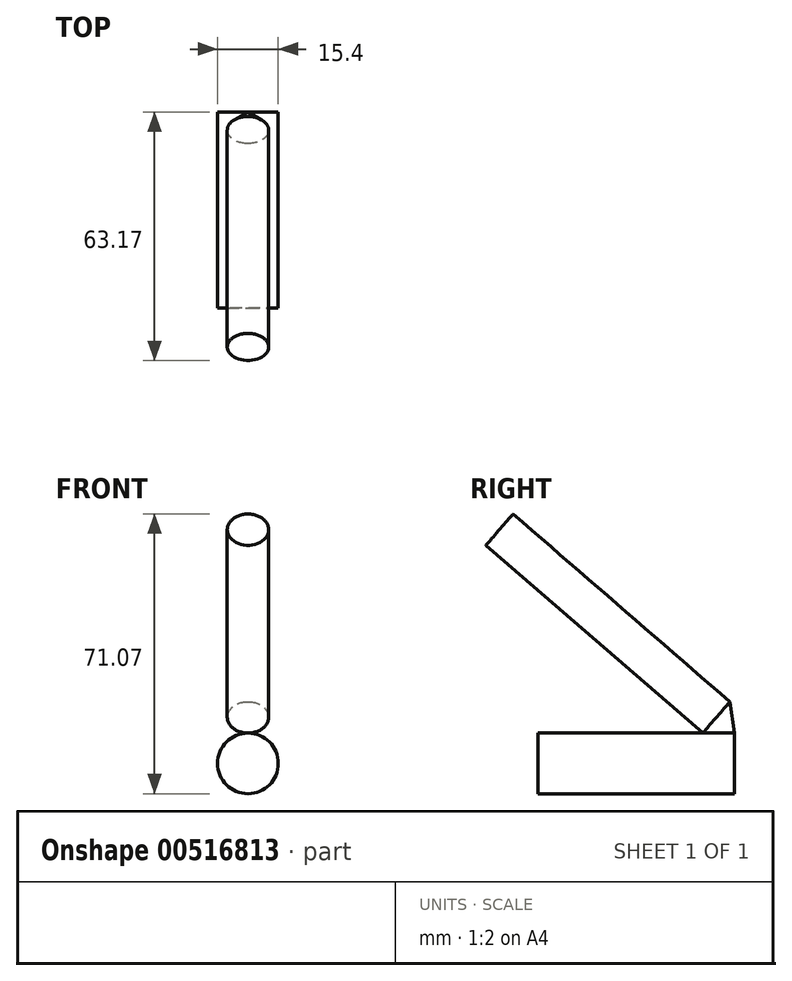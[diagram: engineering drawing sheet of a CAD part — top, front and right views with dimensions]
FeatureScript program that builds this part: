
annotation { "Feature Type Name" : "Feature", "Feature Type Description" : "" }
export const myFeature = defineFeature(function(context is Context, id is Id, definition is map)
    precondition{}
    {
        {
            var Q0;
            Q0=qCreatedBy(makeId("Right.planeOp"),FACE);
            var sketch = newSketch(context, id + "F0", { "sketchPlane" : qUnion([Q0])});
            skLineSegment(sketch, "E0", {"start": v(87.46, -31) * mm, "end": v(37.56, -31) * mm});
            skLineSegment(sketch, "E1", {"start": v(37.56, -31) * mm, "end": v(37.56, -23.3) * mm});
            skLineSegment(sketch, "E2", {"start": v(87.46, -31) * mm, "end": v(87.46, -23.3) * mm});
            skLineSegment(sketch, "E3", {"start": v(37.56, -23.3) * mm, "end": v(87.46, -23.3) * mm});
            skSolve(sketch);
        }
        {
            var Q0;
            Q0 = qSketchRegion(id + "F0", true);
            var Q1;
            Q1=sQuery(id+"F0.wireOp",EDGE,"E0");
            revolve(context, id + "F1", {"entities" : qUnion([Q0]), "axis" : qUnion([Q1]), "revolveType" : RevolveType.FULL});
        }
        {
            var Q0;
            Q0=qCreatedBy(makeId("Right.planeOp"),FACE);
            var sketch = newSketch(context, id + "F2", { "sketchPlane" : qUnion([Q0])});
            skLineSegment(sketch, "E4", {"start": v(87.43, -23.28) * mm, "end": v(27.73, 28.4) * mm});
            skLineSegment(sketch, "E5", {"start": v(87.43, -23.28) * mm, "end": v(79.4, -23.28) * mm});
            skLineSegment(sketch, "E6", {"start": v(79.4, -23.28) * mm, "end": v(24.3, 24.42) * mm});
            skLineSegment(sketch, "E7", {"start": v(27.73, 28.4) * mm, "end": v(24.3, 24.42) * mm});
            skSolve(sketch);
        }
        {
            var Q0;
            Q0=makeQuery(id+"F2.imprint","IMPRINT",FACE,{"disambiguationData":[TD([[makeQuery(id+"F2.imprint","IMPRINT",EDGE,{"derivedFrom":sQuery(id+"F2.wireOp",EDGE,"E4")}),1.0]])]});
            var Q1;
            Q1=sQuery(id+"F2.wireOp",EDGE,"E4");
            revolve(context, id + "F3", {"entities" : qUnion([Q0]), "axis" : qUnion([Q1]), "revolveType" : RevolveType.FULL});
        }
    });
